# Revit family: 874-00-003-DN150-1600
name_source: partatom
category: Pipe Accessories
units: mm (PartAtom-declared; Revit-internal decimal feet)

## family parameters
Always vertical = Yes
Cut with Voids When Loaded = No
Part Type = Valve - Breaks Into
Round Connector Dimension = Use Diameter
Shared = No
Work Plane-Based = No

## types (31) — shared parameters
874-0150-00-14100001 = DN150_PN16
874-0200-00-04100001 = DN200_PN10
874-0200-00-14100001 = DN200_PN16
874-0250-00-04100001 = DN250_PN10
874-0250-00-14100001 = DN250_PN16
874-0300-00-04100001 = DN300_PN10
874-0300-00-14100001 = DN300_PN16
874-0350-00-04100001 = DN350_PN10
874-0350-00-14100001 = DN350_PN16
874-0400-00-04100001 = DN400_PN10
874-0400-00-14100001 = DN400_PN16
874-0450-00-04100001 = DN450_PN10
874-0450-00-14100001 = DN450_PN16
874-0500-00-04100001 = DN500_PN10
874-0500-00-14100001 = DN500_PN16
874-0600-00-04100001 = DN600_PN10
874-0600-00-14100001 = DN600_PN16
874-0700-00-04200001 = DN700_PN10
874-0700-00-14200001 = DN700_PN16
874-0800-00-04200001 = DN800_PN10
874-0800-00-14200001 = DN800_PN16
874-0900-00-04200001 = DN900_PN10
874-0900-00-14200001 = DN900_PN16
874-1000-00-04200001 = DN1000_PN10
874-1000-00-14200001 = DN1000_PN16
874-1200-00-04200001 = DN1200_PN10
874-1200-00-14200001 = DN1200_PN16
874-1400-00-04200001 = DN1400_PN10
874-1400-00-14200001 = DN1400_PN16
874-1600-00-04200001 = DN1600_PN10
874-1600-00-14200001 = DN1600_PN16
Body_Wallthickness = 10 mm  [stored 0.0328084 ft]
Description_ = AVK TILTING DISK CHECK VALVE
Rf_Dia = 3 mm  [stored 0.00984252 ft]
Search_Table = 874-00-003-DN150-1600
URL product pages = https://www.avkvalves.com

## per-type parameters (varying)
- DN0150_PN16: A=163 mm; B=173 mm; C=494 mm; Counter_weight=105 mm  [stored 0.344488 ft]; D=285 mm; D1=211 mm; D1_ref=106 mm; DN=150 mm; DN_ref=130 mm; D_ref=143 mm; Disc_dia=10 mm  [stored 0.0328084 ft]; Disc_dia_ref=5 mm  [stored 0.0164042 ft]; Flange_Thickness=15 mm  [stored 0.0492126 ft]; H=410 mm; H3=300 mm; H_ref=268 mm; H_ref_2=178 mm; ID=75 mm; ID_ref=75 mm; L=210 mm; L_ref=60 mm  [stored 0.19685 ft]; L_ref_2=105 mm  [stored 0.344488 ft]; L_ref_3=42 mm  [stored 0.137795 ft]; L_ref_4=60 mm  [stored 0.19685 ft]; Lever=30 mm  [stored 0.0984252 ft]; Pin=10 mm  [stored 0.0328084 ft]; T=1 mm  [stored 0.00328084 ft]
- DN0200_PN16: A=170 mm; B=202 mm; C=525 mm; Counter_weight=105 mm  [stored 0.344488 ft]; D=340 mm; D1=266 mm; D1_ref=133 mm; DN=200 mm; DN_ref=174 mm; D_ref=170 mm; Disc_dia=216 mm; Disc_dia_ref=108 mm  [stored 0.354331 ft]; Flange_Thickness=15 mm  [stored 0.0492126 ft]; H=460 mm; H3=340 mm; H_ref=290 mm; H_ref_2=193 mm; ID=100 mm  [stored 0.328084 ft]; ID_ref=100 mm  [stored 0.328084 ft]; L=230 mm; L_ref=66 mm  [stored 0.216535 ft]; L_ref_2=115 mm; L_ref_3=46 mm  [stored 0.150919 ft]; L_ref_4=66 mm  [stored 0.216535 ft]; Lever=30 mm  [stored 0.0984252 ft]; Pin=10 mm  [stored 0.0328084 ft]; T=1 mm  [stored 0.00328084 ft]
- DN0250_PN10: A=200 mm; B=230 mm; C=583 mm; Counter_weight=105 mm  [stored 0.344488 ft]; D=395 mm; D1=319 mm; D1_ref=160 mm; DN=250 mm; DN_ref=217 mm; D_ref=198 mm; Disc_dia=200 mm; Disc_dia_ref=100 mm  [stored 0.328084 ft]; Flange_Thickness=15 mm  [stored 0.0492126 ft]; H=512 mm; H3=410 mm; H_ref=315 mm; H_ref_2=210 mm; ID=125 mm; ID_ref=125 mm; L=250 mm; L_ref=71 mm; L_ref_2=125 mm; L_ref_3=50 mm  [stored 0.164042 ft]; L_ref_4=71 mm; Lever=30 mm  [stored 0.0984252 ft]; Pin=10 mm  [stored 0.0328084 ft]; T=44 mm  [stored 0.144357 ft]
- DN0250_PN16: A=200 mm; B=230 mm; C=583 mm; Counter_weight=105 mm  [stored 0.344488 ft]; D=405 mm; D1=319 mm; D1_ref=160 mm; DN=250 mm; DN_ref=217 mm; D_ref=203 mm; Disc_dia=200 mm; Disc_dia_ref=100 mm  [stored 0.328084 ft]; Flange_Thickness=15 mm  [stored 0.0492126 ft]; H=512 mm; H3=410 mm; H_ref=310 mm; H_ref_2=206 mm; ID=125 mm; ID_ref=125 mm; L=250 mm; L_ref=71 mm; L_ref_2=125 mm; L_ref_3=50 mm  [stored 0.164042 ft]; L_ref_4=71 mm; Lever=30 mm  [stored 0.0984252 ft]; Pin=10 mm  [stored 0.0328084 ft]; T=44 mm  [stored 0.144357 ft]
- DN0300_PN10: A=234 mm; B=265 mm; C=667 mm; Counter_weight=140 mm; D=445 mm; D1=370 mm; D1_ref=185 mm; DN=300 mm; DN_ref=261 mm; D_ref=223 mm; Disc_dia=240 mm; Disc_dia_ref=120 mm; Flange_Thickness=20 mm  [stored 0.0656168 ft]; H=637 mm; H3=470 mm; H_ref=415 mm; H_ref_2=276 mm; ID=150 mm; ID_ref=150 mm; L=270 mm; L_ref=77 mm; L_ref_2=135 mm; L_ref_3=54 mm  [stored 0.177165 ft]; L_ref_4=77 mm; Lever=40 mm  [stored 0.131234 ft]; Pin=15 mm  [stored 0.0492126 ft]; T=69 mm  [stored 0.226378 ft]
- DN0300_PN16: A=234 mm; B=265 mm; C=667 mm; Counter_weight=140 mm; D=460 mm; D1=370 mm; D1_ref=185 mm; DN=300 mm; DN_ref=261 mm; D_ref=230 mm; Disc_dia=240 mm; Disc_dia_ref=120 mm; Flange_Thickness=20 mm  [stored 0.0656168 ft]; H=637 mm; H3=470 mm; H_ref=407 mm; H_ref_2=271 mm; ID=150 mm; ID_ref=150 mm; L=270 mm; L_ref=77 mm; L_ref_2=135 mm; L_ref_3=54 mm  [stored 0.177165 ft]; L_ref_4=77 mm; Lever=40 mm  [stored 0.131234 ft]; Pin=15 mm  [stored 0.0492126 ft]; T=69 mm  [stored 0.226378 ft]
- DN0350_PN10: A=260 mm; B=300 mm; C=728 mm; Counter_weight=140 mm; D=505 mm; D1=429 mm; D1_ref=215 mm; DN=350 mm; DN_ref=304 mm; D_ref=253 mm; Disc_dia=280 mm; Disc_dia_ref=140 mm; Flange_Thickness=20 mm  [stored 0.0656168 ft]; H=676 mm; H3=530 mm; H_ref=424 mm; H_ref_2=282 mm; ID=175 mm; ID_ref=175 mm; L=290 mm; L_ref=83 mm; L_ref_2=145 mm; L_ref_3=58 mm; L_ref_4=83 mm; Lever=40 mm  [stored 0.131234 ft]; Pin=15 mm  [stored 0.0492126 ft]; T=101 mm  [stored 0.331365 ft]
- DN0350_PN16: A=260 mm; B=300 mm; C=728 mm; Counter_weight=140 mm; D=520 mm; D1=429 mm; D1_ref=215 mm; DN=350 mm; DN_ref=304 mm; D_ref=260 mm; Disc_dia=280 mm; Disc_dia_ref=140 mm; Flange_Thickness=20 mm  [stored 0.0656168 ft]; H=676 mm; H3=530 mm; H_ref=416 mm; H_ref_2=277 mm; ID=175 mm; ID_ref=175 mm; L=290 mm; L_ref=83 mm; L_ref_2=145 mm; L_ref_3=58 mm; L_ref_4=83 mm; Lever=40 mm  [stored 0.131234 ft]; Pin=15 mm  [stored 0.0492126 ft]; T=101 mm  [stored 0.331365 ft]
- DN0400_PN10: A=290 mm; B=345 mm; C=867 mm; Counter_weight=140 mm; D=565 mm; D1=480 mm; D1_ref=240 mm; DN=400 mm; DN_ref=348 mm; D_ref=283 mm; Disc_dia=330 mm; Disc_dia_ref=165 mm; Flange_Thickness=20 mm  [stored 0.0656168 ft]; H=719 mm; H3=585 mm; H_ref=437 mm; H_ref_2=291 mm; ID=200 mm; ID_ref=200 mm; L=310 mm; L_ref=89 mm; L_ref_2=155 mm; L_ref_3=62 mm  [stored 0.203412 ft]; L_ref_4=89 mm; Lever=40 mm  [stored 0.131234 ft]; Pin=15 mm  [stored 0.0492126 ft]; T=124 mm
- DN0400_PN16: A=290 mm; B=345 mm; C=867 mm; Counter_weight=140 mm; D=580 mm; D1=480 mm; D1_ref=240 mm; DN=400 mm; DN_ref=348 mm; D_ref=290 mm; Disc_dia=330 mm; Disc_dia_ref=165 mm; Flange_Thickness=20 mm  [stored 0.0656168 ft]; H=719 mm; H3=585 mm; H_ref=429 mm; H_ref_2=286 mm; ID=200 mm; ID_ref=200 mm; L=310 mm; L_ref=89 mm; L_ref_2=155 mm; L_ref_3=62 mm  [stored 0.203412 ft]; L_ref_4=89 mm; Lever=40 mm  [stored 0.131234 ft]; Pin=15 mm  [stored 0.0492126 ft]; T=124 mm
- DN0450_PN10: A=328 mm; B=378 mm; C=963 mm; Counter_weight=210 mm; D=615 mm; D1=530 mm; D1_ref=265 mm; DN=450 mm; DN_ref=391 mm; D_ref=308 mm; Disc_dia=360 mm; Disc_dia_ref=180 mm; Flange_Thickness=30 mm  [stored 0.0984252 ft]; H=751 mm; H3=640 mm; H_ref=444 mm; H_ref_2=296 mm; ID=225 mm; ID_ref=225 mm; L=330 mm; L_ref=94 mm  [stored 0.308399 ft]; L_ref_2=165 mm; L_ref_3=66 mm  [stored 0.216535 ft]; L_ref_4=94 mm  [stored 0.308399 ft]; Lever=60 mm  [stored 0.19685 ft]; Pin=25 mm  [stored 0.082021 ft]; T=140 mm
- DN0450_PN16: A=328 mm; B=378 mm; C=963 mm; Counter_weight=210 mm; D=640 mm; D1=548 mm; D1_ref=274 mm; DN=450 mm; DN_ref=391 mm; D_ref=320 mm; Disc_dia=360 mm; Disc_dia_ref=180 mm; Flange_Thickness=30 mm  [stored 0.0984252 ft]; H=751 mm; H3=640 mm; H_ref=431 mm; H_ref_2=287 mm; ID=225 mm; ID_ref=225 mm; L=330 mm; L_ref=94 mm  [stored 0.308399 ft]; L_ref_2=165 mm; L_ref_3=66 mm  [stored 0.216535 ft]; L_ref_4=94 mm  [stored 0.308399 ft]; Lever=60 mm  [stored 0.19685 ft]; Pin=25 mm  [stored 0.082021 ft]; T=140 mm
- DN0500_PN10: A=358 mm; B=405 mm; C=1006 mm; Counter_weight=210 mm; D=670 mm; D1=582 mm; D1_ref=291 mm; DN=500 mm; DN_ref=435 mm; D_ref=335 mm; Disc_dia=410 mm; Disc_dia_ref=205 mm; Flange_Thickness=30 mm  [stored 0.0984252 ft]; H=809 mm; H3=720 mm; H_ref=474 mm; H_ref_2=316 mm; ID=250 mm; ID_ref=250 mm; L=350 mm; L_ref=100 mm  [stored 0.328084 ft]; L_ref_2=175 mm; L_ref_3=70 mm  [stored 0.229659 ft]; L_ref_4=100 mm  [stored 0.328084 ft]; Lever=60 mm  [stored 0.19685 ft]; Pin=25 mm  [stored 0.082021 ft]; T=165 mm
- DN0500_PN16: A=358 mm; B=405 mm; C=1006 mm; Counter_weight=210 mm; D=715 mm; D1=609 mm; D1_ref=305 mm; DN=500 mm; DN_ref=435 mm; D_ref=358 mm; Disc_dia=410 mm; Disc_dia_ref=205 mm; Flange_Thickness=30 mm  [stored 0.0984252 ft]; H=809 mm; H3=720 mm; H_ref=452 mm; H_ref_2=301 mm; ID=250 mm; ID_ref=250 mm; L=350 mm; L_ref=100 mm  [stored 0.328084 ft]; L_ref_2=175 mm; L_ref_3=70 mm  [stored 0.229659 ft]; L_ref_4=100 mm  [stored 0.328084 ft]; Lever=60 mm  [stored 0.19685 ft]; Pin=25 mm  [stored 0.082021 ft]; T=165 mm
- DN0600_PN10: A=420 mm; B=465 mm; C=1180 mm; Counter_weight=210 mm; D=780 mm; D1=682 mm; D1_ref=341 mm; DN=600 mm; DN_ref=522 mm; D_ref=390 mm; Disc_dia=490 mm; Disc_dia_ref=245 mm; Flange_Thickness=30 mm  [stored 0.0984252 ft]; H=1096 mm; H3=840 mm; H_ref=706 mm; H_ref_2=471 mm; ID=300 mm; ID_ref=300 mm; L=390 mm; L_ref=111 mm; L_ref_2=195 mm; L_ref_3=78 mm  [stored 0.255906 ft]; L_ref_4=111 mm; Lever=60 mm  [stored 0.19685 ft]; Pin=25 mm  [stored 0.082021 ft]; T=215 mm
- DN0600_PN16: A=420 mm; B=465 mm; C=1180 mm; Counter_weight=210 mm; D=840 mm; D1=720 mm; D1_ref=360 mm; DN=600 mm; DN_ref=522 mm; D_ref=420 mm; Disc_dia=490 mm; Disc_dia_ref=245 mm; Flange_Thickness=30 mm  [stored 0.0984252 ft]; H=1096 mm; H3=840 mm; H_ref=676 mm; H_ref_2=451 mm; ID=300 mm; ID_ref=300 mm; L=390 mm; L_ref=111 mm; L_ref_2=195 mm; L_ref_3=78 mm  [stored 0.255906 ft]; L_ref_4=111 mm; Lever=60 mm  [stored 0.19685 ft]; Pin=25 mm  [stored 0.082021 ft]; T=215 mm
- DN0700_PN10: A=455 mm; B=515 mm; C=1258 mm; Counter_weight=280 mm; D=895 mm; D1=794 mm; D1_ref=397 mm; DN=700 mm; DN_ref=609 mm; D_ref=448 mm; Disc_dia=580 mm; Disc_dia_ref=290 mm; Flange_Thickness=40 mm  [stored 0.131234 ft]; H=1161 mm; H3=910 mm; H_ref=714 mm; H_ref_2=476 mm; ID=350 mm; ID_ref=350 mm; L=430 mm; L_ref=123 mm; L_ref_2=215 mm; L_ref_3=86 mm  [stored 0.282152 ft]; L_ref_4=123 mm; Lever=80 mm  [stored 0.262467 ft]; Pin=35 mm  [stored 0.114829 ft]; T=255 mm
- DN0700_PN16: A=455 mm; B=515 mm; C=1258 mm; Counter_weight=280 mm; D=910 mm; D1=794 mm; D1_ref=397 mm; DN=700 mm; DN_ref=609 mm; D_ref=455 mm; Disc_dia=580 mm; Disc_dia_ref=290 mm; Flange_Thickness=40 mm  [stored 0.131234 ft]; H=1161 mm; H3=910 mm; H_ref=706 mm; H_ref_2=471 mm; ID=350 mm; ID_ref=350 mm; L=430 mm; L_ref=123 mm; L_ref_2=215 mm; L_ref_3=86 mm  [stored 0.282152 ft]; L_ref_4=123 mm; Lever=80 mm  [stored 0.262467 ft]; Pin=35 mm  [stored 0.114829 ft]; T=255 mm
- DN0800_PN10: A=525 mm; B=560 mm; C=1377 mm; Counter_weight=280 mm; D=1015 mm; D1=901 mm; D1_ref=451 mm; DN=800 mm; DN_ref=696 mm; D_ref=508 mm; Disc_dia=660 mm; Disc_dia_ref=330 mm; Flange_Thickness=40 mm  [stored 0.131234 ft]; H=1241 mm; H3=1030 mm; H_ref=734 mm; H_ref_2=489 mm; ID=400 mm; ID_ref=400 mm; L=470 mm; L_ref=134 mm; L_ref_2=235 mm; L_ref_3=94 mm  [stored 0.308399 ft]; L_ref_4=134 mm; Lever=80 mm  [stored 0.262467 ft]; Pin=35 mm  [stored 0.114829 ft]; T=314 mm
- DN0800_PN16: A=525 mm; B=560 mm; C=1377 mm; Counter_weight=280 mm; D=1025 mm; D1=901 mm; D1_ref=451 mm; DN=800 mm; DN_ref=696 mm; D_ref=513 mm; Disc_dia=660 mm; Disc_dia_ref=330 mm; Flange_Thickness=40 mm  [stored 0.131234 ft]; H=1241 mm; H3=1030 mm; H_ref=729 mm; H_ref_2=486 mm; ID=400 mm; ID_ref=400 mm; L=470 mm; L_ref=134 mm; L_ref_2=235 mm; L_ref_3=94 mm  [stored 0.308399 ft]; L_ref_4=134 mm; Lever=80 mm  [stored 0.262467 ft]; Pin=35 mm  [stored 0.114829 ft]; T=314 mm
- DN0900_PN10: A=597 mm; B=628 mm; C=1515 mm; Counter_weight=315 mm; D=1115 mm; D1=1001 mm; D1_ref=501 mm; DN=900 mm; DN_ref=783 mm; D_ref=558 mm; Disc_dia=740 mm; Disc_dia_ref=370 mm; Flange_Thickness=45 mm  [stored 0.147638 ft]; H=1460 mm; H3=1140 mm; H_ref=903 mm; H_ref_2=602 mm; ID=450 mm; ID_ref=450 mm; L=510 mm; L_ref=146 mm; L_ref_2=255 mm; L_ref_3=102 mm  [stored 0.334646 ft]; L_ref_4=146 mm; Lever=90 mm  [stored 0.295276 ft]; Pin=40 mm  [stored 0.131234 ft]; T=359 mm
- DN0900_PN16: A=597 mm; B=628 mm; C=1515 mm; Counter_weight=315 mm; D=1125 mm; D1=1001 mm; D1_ref=501 mm; DN=900 mm; DN_ref=783 mm; D_ref=563 mm; Disc_dia=740 mm; Disc_dia_ref=370 mm; Flange_Thickness=45 mm  [stored 0.147638 ft]; H=1460 mm; H3=1140 mm; H_ref=898 mm; H_ref_2=598 mm; ID=450 mm; ID_ref=450 mm; L=510 mm; L_ref=146 mm; L_ref_2=255 mm; L_ref_3=102 mm  [stored 0.334646 ft]; L_ref_4=146 mm; Lever=90 mm  [stored 0.295276 ft]; Pin=40 mm  [stored 0.131234 ft]; T=359 mm
- DN1000_PN10: A=690 mm; B=730 mm; C=1812 mm; Counter_weight=350 mm; D=1230 mm; D1=1112 mm; D1_ref=556 mm; DN=1000 mm; DN_ref=870 mm; D_ref=615 mm; Disc_dia=830 mm; Disc_dia_ref=415 mm; Flange_Thickness=50 mm  [stored 0.164042 ft]; H=1633 mm; H3=1260 mm; H_ref=1018 mm; H_ref_2=679 mm; ID=500 mm; ID_ref=500 mm; L=550 mm; L_ref=157 mm; L_ref_2=275 mm; L_ref_3=110 mm; L_ref_4=157 mm; Lever=100 mm  [stored 0.328084 ft]; Pin=45 mm  [stored 0.147638 ft]; T=405 mm
- DN1000_PN16: A=690 mm; B=730 mm; C=1812 mm; Counter_weight=350 mm; D=1255 mm; D1=1112 mm; D1_ref=556 mm; DN=1000 mm; DN_ref=870 mm; D_ref=628 mm; Disc_dia=830 mm; Disc_dia_ref=415 mm; Flange_Thickness=50 mm  [stored 0.164042 ft]; H=1633 mm; H3=1260 mm; H_ref=1006 mm; H_ref_2=670 mm; ID=500 mm; ID_ref=500 mm; L=550 mm; L_ref=157 mm; L_ref_2=275 mm; L_ref_3=110 mm; L_ref_4=157 mm; Lever=100 mm  [stored 0.328084 ft]; Pin=45 mm  [stored 0.147638 ft]; T=405 mm
- DN1200_PN10: A=820 mm; B=860 mm; C=2071 mm; Counter_weight=420 mm; D=1455 mm; D1=1328 mm; D1_ref=664 mm; DN=1200 mm; DN_ref=1043 mm; D_ref=728 mm; Disc_dia=1060 mm; Disc_dia_ref=530 mm; Flange_Thickness=60 mm  [stored 0.19685 ft]; H=1878 mm; H3=1495 mm; H_ref=1151 mm; H_ref_2=767 mm; ID=600 mm; ID_ref=480 mm; L=630 mm; L_ref=180 mm; L_ref_2=315 mm; L_ref_3=126 mm; L_ref_4=180 mm; Lever=120 mm; Pin=55 mm  [stored 0.180446 ft]; T=530 mm
- DN1200_PN16: A=820 mm; B=860 mm; C=2071 mm; Counter_weight=420 mm; D=1485 mm; D1=1328 mm; D1_ref=664 mm; DN=1200 mm; DN_ref=1044 mm; D_ref=743 mm; Disc_dia=1060 mm; Disc_dia_ref=530 mm; Flange_Thickness=60 mm  [stored 0.19685 ft]; H=1878 mm; H3=1495 mm; H_ref=1136 mm; H_ref_2=757 mm; ID=600 mm; ID_ref=480 mm; L=630 mm; L_ref=180 mm; L_ref_2=315 mm; L_ref_3=126 mm; L_ref_4=180 mm; Lever=120 mm; Pin=55 mm  [stored 0.180446 ft]; T=530 mm
- DN1400_PN10: A=905 mm; B=950 mm; C=2252 mm; Counter_weight=455 mm; D=1675 mm; D1=1530 mm; D1_ref=765 mm; DN=1400 mm; DN_ref=1217 mm; D_ref=838 mm; Disc_dia=1240 mm; Disc_dia_ref=620 mm; Flange_Thickness=65 mm  [stored 0.213255 ft]; H=2026 mm; H3=1695 mm; H_ref=1189 mm; H_ref_2=792 mm; ID=700 mm; ID_ref=570 mm; L=710 mm; L_ref=203 mm; L_ref_2=355 mm; L_ref_3=142 mm; L_ref_4=203 mm; Lever=130 mm; Pin=60 mm  [stored 0.19685 ft]; T=617 mm
- DN1400_PN16: A=905 mm; B=950 mm; C=2252 mm; Counter_weight=455 mm; D=1685 mm; D1=1530 mm; D1_ref=765 mm; DN=1400 mm; DN_ref=1217 mm; D_ref=843 mm; Disc_dia=1240 mm; Disc_dia_ref=620 mm; Flange_Thickness=65 mm  [stored 0.213255 ft]; H=2026 mm; H3=1695 mm; H_ref=1184 mm; H_ref_2=789 mm; ID=700 mm; ID_ref=570 mm; L=710 mm; L_ref=203 mm; L_ref_2=355 mm; L_ref_3=142 mm; L_ref_4=203 mm; Lever=130 mm; Pin=60 mm  [stored 0.19685 ft]; T=617 mm
- DN1600_PN10: A=1015 mm; B=1075 mm; C=2504 mm; Counter_weight=490 mm; D=1915 mm; D1=1750 mm; D1_ref=875 mm; DN=1600 mm; DN_ref=1391 mm; D_ref=958 mm; Disc_dia=1420 mm; Disc_dia_ref=710 mm; Flange_Thickness=70 mm  [stored 0.229659 ft]; H=2234 mm; H3=1945 mm; H_ref=1277 mm; H_ref_2=851 mm; ID=800 mm; ID_ref=660 mm; L=790 mm; L_ref=226 mm; L_ref_2=395 mm; L_ref_3=158 mm; L_ref_4=226 mm; Lever=140 mm; Pin=65 mm  [stored 0.213255 ft]; T=648 mm
- DN1600_PN16: A=1015 mm; B=1075 mm; C=2504 mm; Counter_weight=490 mm; D=1930 mm; D1=1750 mm; D1_ref=875 mm; DN=1600 mm; DN_ref=1391 mm; D_ref=965 mm; Disc_dia=1420 mm; Disc_dia_ref=710 mm; Flange_Thickness=70 mm  [stored 0.229659 ft]; H=2234 mm; H3=1945 mm; H_ref=1269 mm; H_ref_2=846 mm; ID=800 mm; ID_ref=660 mm; L=790 mm; L_ref=226 mm; L_ref_2=395 mm; L_ref_3=158 mm; L_ref_4=226 mm; Lever=140 mm; Pin=65 mm  [stored 0.213255 ft]; T=648 mm
- DN0200_PN10: A=170 mm; B=202 mm; C=525 mm; Counter_weight=105 mm  [stored 0.344488 ft]; D=340 mm; D1=266 mm; D1_ref=133 mm; DN=200 mm; DN_ref=174 mm; D_ref=170 mm; Disc_dia=10 mm  [stored 0.0328084 ft]; Disc_dia_ref=5 mm  [stored 0.0164042 ft]; Flange_Thickness=15 mm  [stored 0.0492126 ft]; H=460 mm; H3=340 mm; H_ref=290 mm; H_ref_2=193 mm; ID=100 mm  [stored 0.328084 ft]; ID_ref=100 mm  [stored 0.328084 ft]; L=230 mm; L_ref=66 mm  [stored 0.216535 ft]; L_ref_2=115 mm; L_ref_3=46 mm  [stored 0.150919 ft]; L_ref_4=66 mm  [stored 0.216535 ft]; Lever=30 mm  [stored 0.0984252 ft]; Pin=10 mm  [stored 0.0328084 ft]; T=1 mm  [stored 0.00328084 ft]

note: [stored X ft] marks values corroborated as IEEE doubles in the binary element streams (Revit-internal decimal feet)

## geometry (parser evidence)
native form markers: Sweep x5
no freeform markers — native parametric forms only
